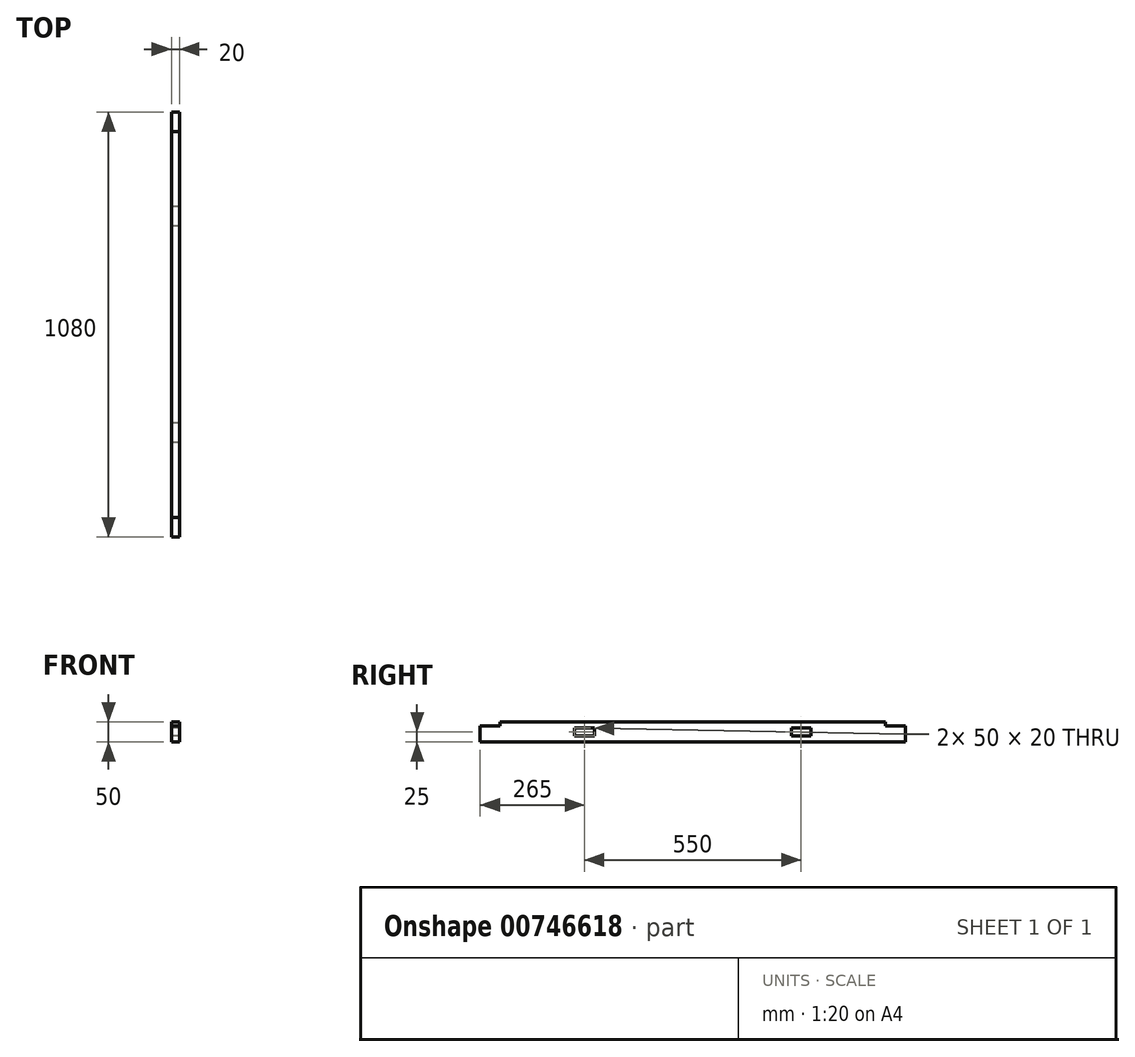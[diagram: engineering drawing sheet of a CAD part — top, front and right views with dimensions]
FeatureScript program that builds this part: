
annotation { "Feature Type Name" : "Feature", "Feature Type Description" : "" }
export const myFeature = defineFeature(function(context is Context, id is Id, definition is map)
    precondition{}
    {
        {
            var Q0;
            Q0=qCreatedBy(makeId("Front.planeOp"),FACE);
            var sketch = newSketch(context, id + "F0", { "sketchPlane" : qUnion([Q0])});
            skLineSegment(sketch, "E0.bottom", {"start": v(-10, 25) * mm, "end": v(10, 25) * mm});
            skLineSegment(sketch, "E0.top", {"start": v(-10, -25) * mm, "end": v(10, -25) * mm});
            skLineSegment(sketch, "E0.left", {"start": v(-10, 25) * mm, "end": v(-10, -25) * mm});
            skLineSegment(sketch, "E0.right", {"start": v(10, 25) * mm, "end": v(10, -25) * mm});
            skPoint(sketch, "E0.middle", {"position": v(0, 0) * mm});
            skSolve(sketch);
        }
        {
            var Q0;
            Q0 = qSketchRegion(id + "F0", true);
            extrude(context, id + "F1", {"entities" : qUnion([Q0]), "oppositeDirection" : true, "depth" : 1080 * mm, "offsetDistance" : 25 * mm});
        }
        {
            var Q0;
            Q0=makeQuery(id+"F1.opExtrude","SWEPT_FACE",FACE,{"disambiguationData":[OSD([sQuery(id+"F0.wireOp",EDGE,"E0.left")])]});
            var sketch = newSketch(context, id + "F2", { "sketchPlane" : qUnion([Q0])});
            skLineSegment(sketch, "E1.bottom", {"start": v(-790, -10) * mm, "end": v(-840, -10) * mm});
            skLineSegment(sketch, "E1.top", {"start": v(-790, 10) * mm, "end": v(-840, 10) * mm});
            skLineSegment(sketch, "E1.left", {"start": v(-790, -10) * mm, "end": v(-790, 10) * mm});
            skLineSegment(sketch, "E1.right", {"start": v(-840, -10) * mm, "end": v(-840, 10) * mm});
            skPoint(sketch, "E1.middle", {"position": v(-815, 0) * mm});
            skLineSegment(sketch, "E2.bottom", {"start": v(-240, -10) * mm, "end": v(-290, -10) * mm});
            skLineSegment(sketch, "E2.top", {"start": v(-240, 10) * mm, "end": v(-290, 10) * mm});
            skLineSegment(sketch, "E2.left", {"start": v(-240, -10) * mm, "end": v(-240, 10) * mm});
            skLineSegment(sketch, "E2.right", {"start": v(-290, -10) * mm, "end": v(-290, 10) * mm});
            skPoint(sketch, "E2.middle", {"position": v(-265, 0) * mm});
            skSolve(sketch);
        }
        {
            var Q0;
            Q0 = qSketchRegion(id + "F2", true);
            extrude(context, id + "F3", {"entities" : qUnion([Q0]), "operationType" : NewBodyOperationType.REMOVE, "endBound" : BoundingType.THROUGH_ALL, "oppositeDirection" : true, "depth" : 25 * mm, "offsetDistance" : 25 * mm});
        }
        {
            var Q0;
            Q0=makeQuery(id+"F1.opExtrude","CAP_FACE",FACE,{"disambiguationData":[OSD([sQuery(id+"F0.wireOp",EDGE,"E0.bottom"),sQuery(id+"F0.wireOp",EDGE,"E0.top"),sQuery(id+"F0.wireOp",EDGE,"E0.left"),sQuery(id+"F0.wireOp",EDGE,"E0.right")])],"isStart":true});
            var sketch = newSketch(context, id + "F4", { "sketchPlane" : qUnion([Q0])});
            skLineSegment(sketch, "E3.bottom", {"start": v(-10, 25) * mm, "end": v(10, 25) * mm});
            skLineSegment(sketch, "E3.top", {"start": v(-10, 15) * mm, "end": v(10, 15) * mm});
            skLineSegment(sketch, "E3.left", {"start": v(-10, 25) * mm, "end": v(-10, 15) * mm});
            skLineSegment(sketch, "E3.right", {"start": v(10, 25) * mm, "end": v(10, 15) * mm});
            skSolve(sketch);
        }
        {
            var Q0;
            Q0=makeQuery(id+"F4.imprint","IMPRINT",FACE,{"disambiguationData":[TD([[makeQuery(id+"F4.imprint","IMPRINT",EDGE,{"derivedFrom":sQuery(id+"F4.wireOp",EDGE,"E3.bottom")}),-1.0]])]});
            extrude(context, id + "F5", {"entities" : qUnion([Q0]), "operationType" : NewBodyOperationType.REMOVE, "oppositeDirection" : true, "depth" : 50 * mm, "offsetDistance" : 25 * mm});
        }
        {
            var Q0;
            Q0=makeQuery(id+"F1.opExtrude","CAP_FACE",FACE,{"disambiguationData":[OSD([sQuery(id+"F0.wireOp",EDGE,"E0.bottom"),sQuery(id+"F0.wireOp",EDGE,"E0.top"),sQuery(id+"F0.wireOp",EDGE,"E0.left"),sQuery(id+"F0.wireOp",EDGE,"E0.right")])],"isStart":false});
            var sketch = newSketch(context, id + "F6", { "sketchPlane" : qUnion([Q0])});
            skLineSegment(sketch, "E4.bottom", {"start": v(-10, 25) * mm, "end": v(10, 25) * mm});
            skLineSegment(sketch, "E4.top", {"start": v(-10, 15) * mm, "end": v(10, 15) * mm});
            skLineSegment(sketch, "E4.left", {"start": v(-10, 25) * mm, "end": v(-10, 15) * mm});
            skLineSegment(sketch, "E4.right", {"start": v(10, 25) * mm, "end": v(10, 15) * mm});
            skSolve(sketch);
        }
        {
            var Q0;
            Q0=makeQuery(id+"F6.imprint","IMPRINT",FACE,{"disambiguationData":[TD([[makeQuery(id+"F6.imprint","IMPRINT",EDGE,{"derivedFrom":sQuery(id+"F6.wireOp",EDGE,"E4.bottom")}),1.0]])]});
            extrude(context, id + "F7", {"entities" : qUnion([Q0]), "operationType" : NewBodyOperationType.REMOVE, "oppositeDirection" : true, "depth" : 50 * mm, "offsetDistance" : 25 * mm});
        }
    });
